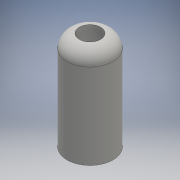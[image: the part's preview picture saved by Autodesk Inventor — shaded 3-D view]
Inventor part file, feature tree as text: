
AUTODESK INVENTOR PART (.ipt)
format: ipt  version: 2016 (Build 200138000, 138)  size: 108,032 bytes
history: native  units: mm
features: extrude x1, fillet x1, hole x1, sketch x1
ambient origin geometry x8: Origin, YZ Plane, XZ Plane, XY Plane, X Axis, Y Axis, Z Axis, Center Point
bodies: Solid1 (feature_tree)
feature tree (4):
  extrude  "Extrusion1"  Depth=2.0mm TaperAngle=0.0deg
  fillet  "Fillet1"  Radius=2.0mm
  hole  "Hole1"  [1 undecoded]
  sketch  "Sketch1"  dims[d0=7.0mm d1=15.0mm d2=0.0mm d3=2.0mm d13=10.0mm d14=10.0mm d6=3.25mm d7=6.0mm d8=4.0mm d9=2.0mm d10=90.0deg d11=8.0mm d12=20.594885mm]
note: 1 required parameter value undecoded (feature->parameter linkage not recoverable at this tier; creation-order binding heuristic only, values carry confidence <= 0.55)
